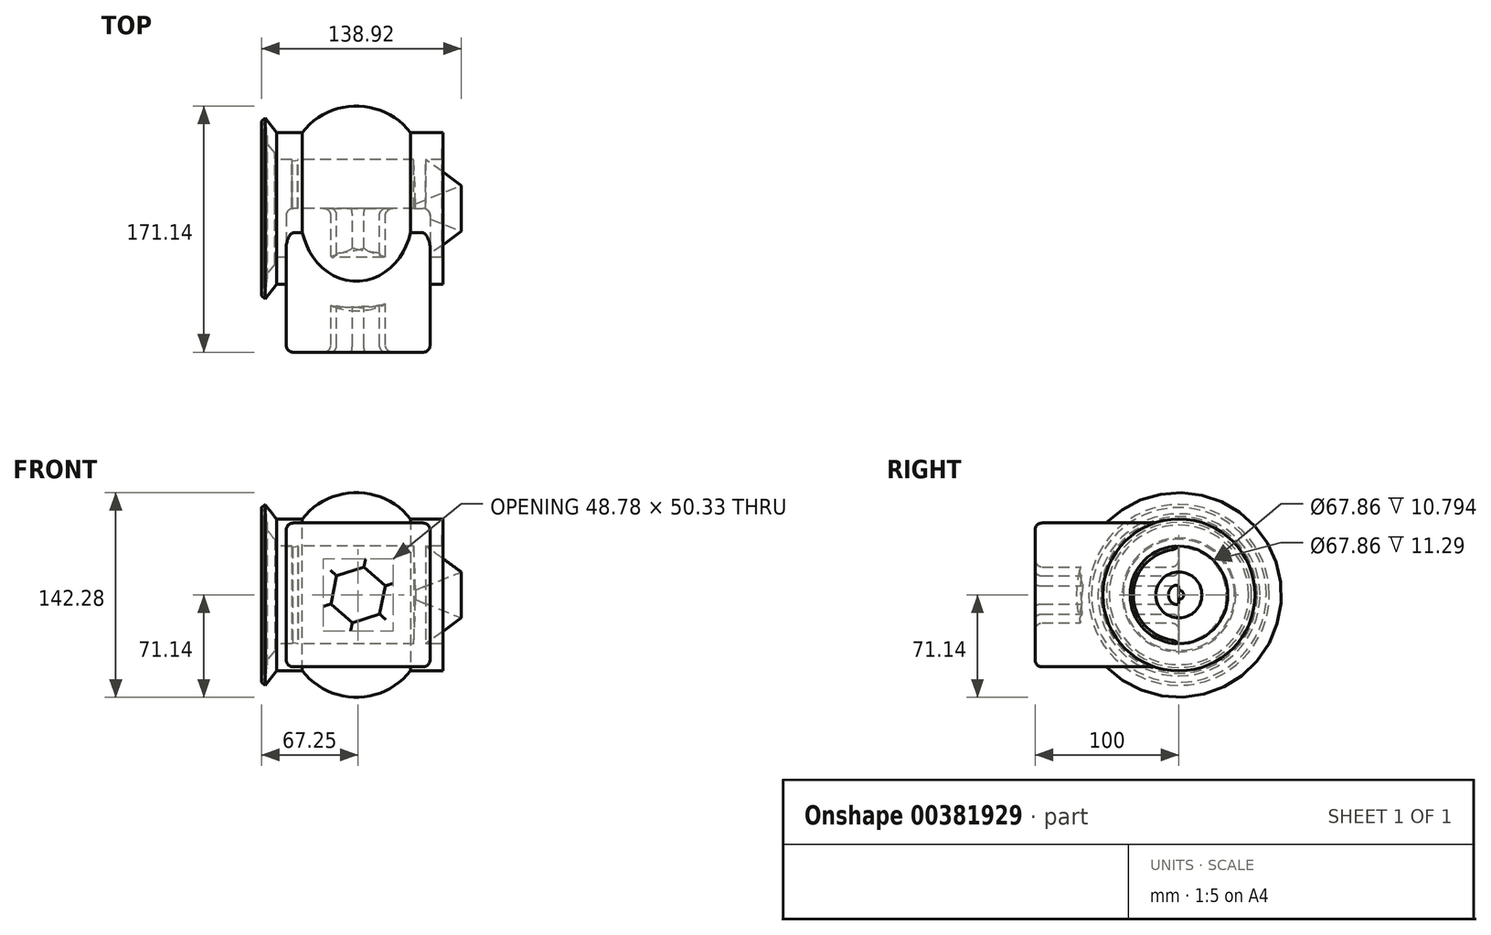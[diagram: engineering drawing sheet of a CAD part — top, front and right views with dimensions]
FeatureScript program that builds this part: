
annotation { "Feature Type Name" : "Feature", "Feature Type Description" : "" }
export const myFeature = defineFeature(function(context is Context, id is Id, definition is map)
    precondition{}
    {
        {
            var Q0;
            Q0=qCreatedBy(makeId("Front.planeOp"),FACE);
            var sketch = newSketch(context, id + "F0", { "sketchPlane" : qUnion([Q0])});
            skLineSegment(sketch, "E0.bottom", {"start": v(-50, 50) * mm, "end": v(50, 50) * mm});
            skLineSegment(sketch, "E0.top", {"start": v(-50, -50) * mm, "end": v(50, -50) * mm});
            skLineSegment(sketch, "E0.left", {"start": v(-50, 50) * mm, "end": v(-50, -50) * mm});
            skLineSegment(sketch, "E0.right", {"start": v(50, 50) * mm, "end": v(50, -50) * mm});
            skPoint(sketch, "E0.middle", {"position": v(0, 0) * mm});
            skSolve(sketch);
        }
        {
            var Q0;
            Q0 = qSketchRegion(id + "F0", true);
            extrude(context, id + "F1", {"entities" : qUnion([Q0]), "depth" : 100 * mm});
        }
        {
            var Q0;
            Q0=qCreatedBy(makeId("Front.planeOp"),FACE);
            var sketch = newSketch(context, id + "F2", { "sketchPlane" : qUnion([Q0])});
            skCircle(sketch, "E1.cCircle", {"center": v(0, 0) * mm, "radius": 19.92 * mm, "construction": true});
            skLineSegment(sketch, "E1.0", {"start": v(-14.88, 13.25) * mm, "end": v(4.03, 19.5) * mm});
            skLineSegment(sketch, "E1.1", {"start": v(4.03, 19.5) * mm, "end": v(18.91, 6.26) * mm});
            skLineSegment(sketch, "E1.2", {"start": v(18.91, 6.26) * mm, "end": v(14.88, -13.25) * mm});
            skLineSegment(sketch, "E1.3", {"start": v(14.88, -13.25) * mm, "end": v(-4.03, -19.5) * mm});
            skLineSegment(sketch, "E1.4", {"start": v(-4.03, -19.5) * mm, "end": v(-18.91, -6.26) * mm});
            skLineSegment(sketch, "E1.5", {"start": v(-18.91, -6.26) * mm, "end": v(-14.88, 13.25) * mm});
            skSolve(sketch);
        }
        {
            var Q0;
            Q0 = qSketchRegion(id + "F2", true);
            extrude(context, id + "F3", {"entities" : qUnion([Q0]), "operationType" : NewBodyOperationType.REMOVE, "endBound" : BoundingType.THROUGH_ALL, "depth" : 45 * mm});
        }
        {
            var Q0;
            Q0=makeQuery(id+"F1.opExtrude","CAP_EDGE",EDGE,{"disambiguationData":[OSD([sQuery(id+"F0.wireOp",EDGE,"E0.bottom")])],"isStart":false});
            var Q1;
            Q1=makeQuery(id+"F1.opExtrude","SWEPT_FACE",FACE,{"disambiguationData":[OSD([sQuery(id+"F0.wireOp",EDGE,"E0.bottom")])]});
            var Q2;
            Q2=makeQuery(id+"F1.opExtrude","SWEPT_FACE",FACE,{"disambiguationData":[OSD([sQuery(id+"F0.wireOp",EDGE,"E0.right")])]});
            var Q3;
            Q3=makeQuery(id+"F1.opExtrude","CAP_FACE",FACE,{"disambiguationData":[OSD([sQuery(id+"F0.wireOp",EDGE,"E0.bottom"),sQuery(id+"F0.wireOp",EDGE,"E0.top"),sQuery(id+"F0.wireOp",EDGE,"E0.left"),sQuery(id+"F0.wireOp",EDGE,"E0.right")])],"isStart":false});
            var Q4;
            Q4=makeQuery(id+"F1.opExtrude","CAP_FACE",FACE,{"disambiguationData":[OSD([sQuery(id+"F0.wireOp",EDGE,"E0.bottom"),sQuery(id+"F0.wireOp",EDGE,"E0.top"),sQuery(id+"F0.wireOp",EDGE,"E0.left"),sQuery(id+"F0.wireOp",EDGE,"E0.right")])],"isStart":true});
            var Q5;
            Q5=makeQuery(id+"F1.opExtrude","SWEPT_FACE",FACE,{"disambiguationData":[OSD([sQuery(id+"F0.wireOp",EDGE,"E0.top")])]});
            fillet(context, id + "F4", {"entities" : qUnion([Q0, Q1, Q2, Q3, Q4, Q5]), "radius" : 5 * mm, "tangentPropagation" : true, "allowEdgeOverflow" : false});
        }
        {
            var Q0;
            Q0=qCreatedBy(makeId("Front.planeOp"),FACE);
            var sketch = newSketch(context, id + "F5", { "sketchPlane" : qUnion([Q0])});
            skLineSegment(sketch, "E2", {"start": v(-68.95, 0) * mm, "end": v(61.15, 0) * mm, "construction": true});
            skArc(sketch, "E3", {"start": v(38.29, 50.08) * mm, "mid": v(-1.32, 71.14) * mm, "end": v(-40.83, 49.9) * mm});
            skLineSegment(sketch, "E4", {"start": v(-40.83, 49.9) * mm, "end": v(38.29, 50.08) * mm});
            skLineSegment(sketch, "E5", {"start": v(38.47, 40.1) * mm, "end": v(71.67, 15.97) * mm});
            skLineSegment(sketch, "E6", {"start": v(71.67, 15.97) * mm, "end": v(39.92, 3.27) * mm});
            skLineSegment(sketch, "E7", {"start": v(39.92, 3.27) * mm, "end": v(38.47, 40.1) * mm});
            skLineSegment(sketch, "E8", {"start": v(-41.73, 33.75) * mm, "end": v(-64.6, 62.78) * mm});
            skLineSegment(sketch, "E9", {"start": v(-64.6, 62.78) * mm, "end": v(-67.25, 60.69) * mm});
            skLineSegment(sketch, "E10", {"start": v(-67.25, 60.69) * mm, "end": v(-45.46, 33.02) * mm});
            skLineSegment(sketch, "E11", {"start": v(-45.46, 33.02) * mm, "end": v(-41.73, 33.75) * mm});
            skLineSegment(sketch, "E12", {"start": v(-63.83, 56.34) * mm, "end": v(-66.3, 54.38) * mm});
            skLineSegment(sketch, "E13", {"start": v(-66.3, 54.38) * mm, "end": v(-51.4, 35.46) * mm});
            skLineSegment(sketch, "E14", {"start": v(-51.4, 35.46) * mm, "end": v(-46.27, 39.5) * mm});
            skLineSegment(sketch, "E15", {"start": v(-46.27, 39.5) * mm, "end": v(-63.83, 56.34) * mm});
            skLineSegment(sketch, "E16", {"start": v(-61.88, 51.53) * mm, "end": v(-65.76, 48.48) * mm});
            skLineSegment(sketch, "E17", {"start": v(-65.76, 48.48) * mm, "end": v(-58.02, 38.65) * mm});
            skLineSegment(sketch, "E18", {"start": v(-58.02, 38.65) * mm, "end": v(-53.01, 42.6) * mm});
            skLineSegment(sketch, "E19", {"start": v(-53.01, 42.6) * mm, "end": v(-61.88, 51.53) * mm});
            skLineSegment(sketch, "E20", {"start": v(-56.98, -33.93) * mm, "end": v(58.25, -33.93) * mm});
            skLineSegment(sketch, "E21", {"start": v(-56.98, -33.93) * mm, "end": v(-56.98, -52.8) * mm});
            skLineSegment(sketch, "E22", {"start": v(-56.98, -52.8) * mm, "end": v(58.8, -52.8) * mm});
            skLineSegment(sketch, "E23", {"start": v(58.8, -52.8) * mm, "end": v(58.25, -33.93) * mm});
            skSolve(sketch);
        }
        {
            var Q0;
            Q0 = qSketchRegion(id + "F5", true);
            var Q1;
            Q1=sQuery(id+"F5.wireOp",EDGE,"E2");
            revolve(context, id + "F6", {"operationType" : NewBodyOperationType.ADD, "entities" : qUnion([Q0]), "axis" : qUnion([Q1]), "revolveType" : RevolveType.FULL});
        }
    });
